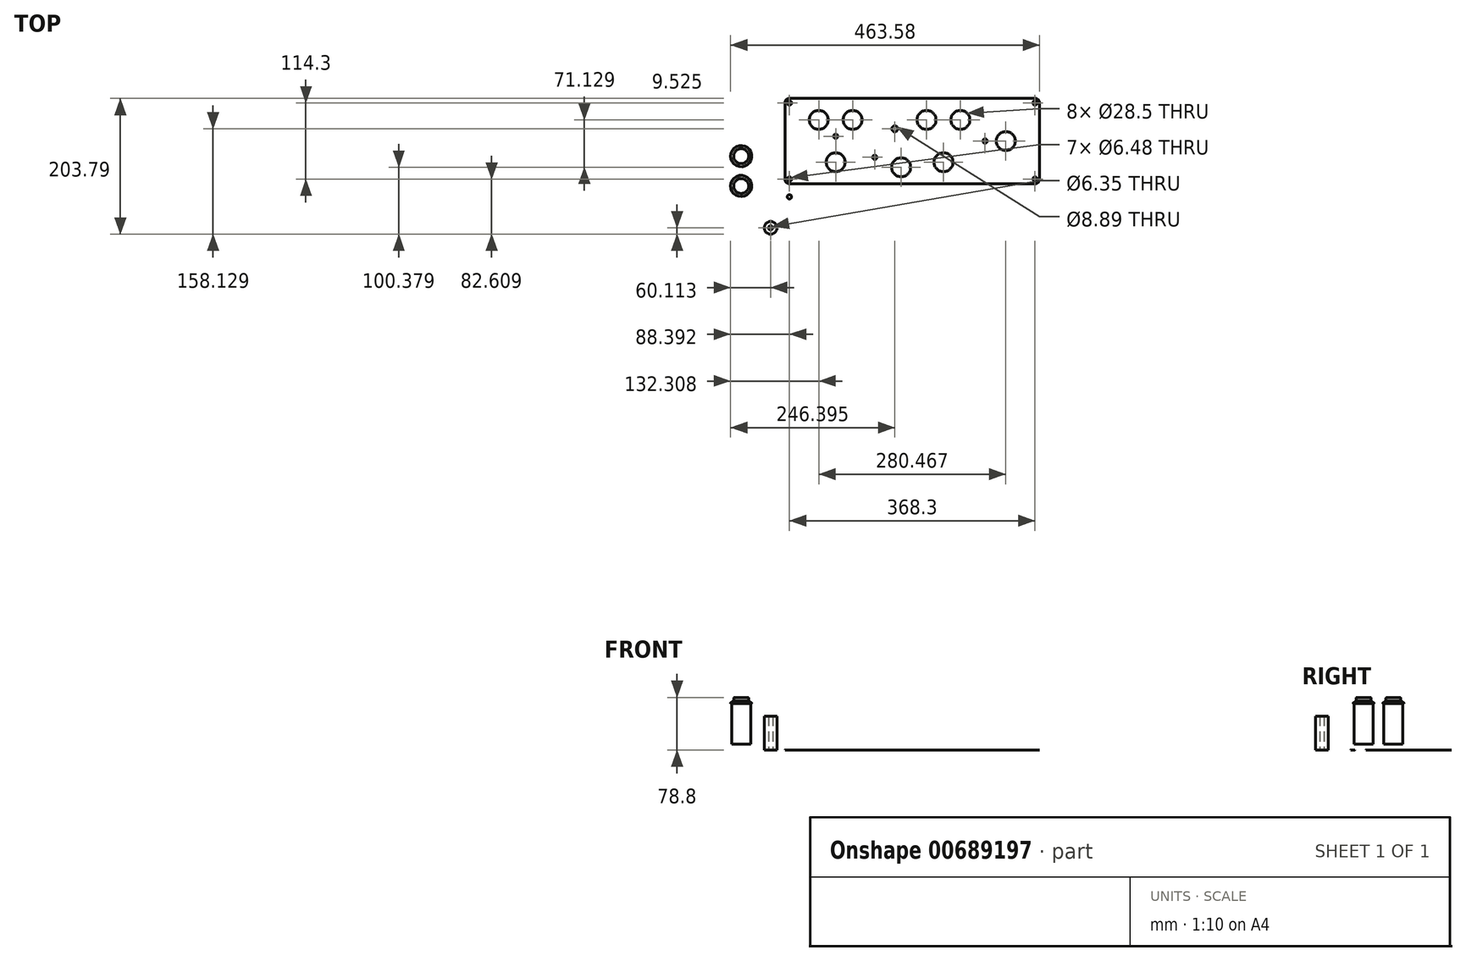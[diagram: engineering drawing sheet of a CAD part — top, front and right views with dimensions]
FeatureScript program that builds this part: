
annotation { "Feature Type Name" : "Feature", "Feature Type Description" : "" }
export const myFeature = defineFeature(function(context is Context, id is Id, definition is map)
    precondition{}
    {
        {
            assignVariable(context, id + "F0", {"name" : "standoff_length", "anyValue" : 50.8 * mm});
        }
        {
            var Q0;
            Q0=qCreatedBy(makeId("Top.planeOp"),FACE);
            var sketch = newSketch(context, id + "F1", { "sketchPlane" : qUnion([Q0])});
            skLineSegment(sketch, "E0.bottom", {"start": v(-110.66, 131.44) * mm, "end": v(271.4, 131.44) * mm});
            skLineSegment(sketch, "E0.top", {"start": v(-110.66, 3.38) * mm, "end": v(271.4, 3.38) * mm});
            skLineSegment(sketch, "E0.left", {"start": v(-110.66, 131.44) * mm, "end": v(-110.66, 3.38) * mm});
            skLineSegment(sketch, "E0.right", {"start": v(271.4, 131.44) * mm, "end": v(271.4, 3.38) * mm});
            skPoint(sketch, "E0.middle", {"position": v(80.37, 67.4) * mm});
            skCircle(sketch, "E1", {"center": v(220.6, 67.4) * mm, "radius": 14.25 * mm});
            skPoint(sketch, "E2", {"position": v(271.4, 67.4) * mm});
            skCircle(sketch, "E3", {"center": v(101.81, 99.16) * mm, "radius": 14.25 * mm});
            skCircle(sketch, "E4", {"center": v(152.61, 99.16) * mm, "radius": 14.25 * mm});
            skCircle(sketch, "E5", {"center": v(127.21, 35.66) * mm, "radius": 14.25 * mm});
            skLineSegment(sketch, "E6", {"start": v(101.81, 99.16) * mm, "end": v(127.21, 35.66) * mm, "construction": true});
            skLineSegment(sketch, "E7", {"start": v(152.61, 99.16) * mm, "end": v(127.21, 35.66) * mm, "construction": true});
            skLineSegment(sketch, "E8", {"start": v(101.81, 99.16) * mm, "end": v(152.61, 99.16) * mm, "construction": true});
            skPoint(sketch, "E9", {"position": v(127.21, 99.16) * mm});
            skCircle(sketch, "E10", {"center": v(63.71, 28.03) * mm, "radius": 14.25 * mm});
            skLineSegment(sketch, "E11", {"start": v(127.21, 99.16) * mm, "end": v(127.21, 35.66) * mm, "construction": true});
            skPoint(sketch, "E12", {"position": v(127.21, 67.4) * mm});
            skLineSegment(sketch, "E13.bottom", {"start": v(-110.66, -137.4) * mm, "end": v(271.4, -137.4) * mm});
            skLineSegment(sketch, "E13.top", {"start": v(-110.66, -9.32) * mm, "end": v(271.4, -9.32) * mm});
            skLineSegment(sketch, "E13.left", {"start": v(-110.66, -137.4) * mm, "end": v(-110.66, -9.32) * mm});
            skLineSegment(sketch, "E13.right", {"start": v(271.4, -137.4) * mm, "end": v(271.4, -9.32) * mm});
            skPoint(sketch, "E13.middle", {"position": v(80.37, -73.36) * mm});
            skLineSegment(sketch, "E14.bottom", {"start": v(-103.78, 124.56) * mm, "end": v(264.52, 124.56) * mm, "construction": true});
            skLineSegment(sketch, "E14.top", {"start": v(-103.78, 10.26) * mm, "end": v(264.52, 10.26) * mm, "construction": true});
            skLineSegment(sketch, "E14.left", {"start": v(-103.78, 124.56) * mm, "end": v(-103.78, 10.26) * mm, "construction": true});
            skLineSegment(sketch, "E14.right", {"start": v(264.52, 124.56) * mm, "end": v(264.52, 10.26) * mm, "construction": true});
            skCircle(sketch, "E15", {"center": v(-103.78, 124.56) * mm, "radius": 3.24 * mm});
            skCircle(sketch, "E16", {"center": v(-103.78, 10.26) * mm, "radius": 3.24 * mm});
            skCircle(sketch, "E17", {"center": v(264.52, 10.26) * mm, "radius": 3.24 * mm});
            skCircle(sketch, "E18", {"center": v(264.52, 124.56) * mm, "radius": 3.24 * mm});
            skLineSegment(sketch, "E19.bottom", {"start": v(-110.66, 3.38) * mm, "end": v(271.4, 3.38) * mm, "construction": true});
            skLineSegment(sketch, "E19.top", {"start": v(-110.66, -9.32) * mm, "end": v(271.4, -9.32) * mm, "construction": true});
            skLineSegment(sketch, "E19.left", {"start": v(-110.66, 3.38) * mm, "end": v(-110.66, -9.32) * mm, "construction": true});
            skLineSegment(sketch, "E19.right", {"start": v(271.4, 3.38) * mm, "end": v(271.4, -9.32) * mm, "construction": true});
            skLineSegment(sketch, "E20", {"start": v(-110.66, -2.97) * mm, "end": v(271.4, -2.97) * mm, "construction": true});
            skCircle(sketch, "E21.MirrorC", {"center": v(-103.78, -16.2) * mm, "radius": 3.24 * mm});
            skCircle(sketch, "E22.MirrorC", {"center": v(-103.78, -130.5) * mm, "radius": 3.24 * mm});
            skCircle(sketch, "E23.MirrorC", {"center": v(264.52, -130.5) * mm, "radius": 3.24 * mm});
            skCircle(sketch, "E24.MirrorC", {"center": v(264.52, -16.2) * mm, "radius": 3.24 * mm});
            skArc(sketch, "E25", {"start": v(-103.78, 131.44) * mm, "mid": v(-108.65, 129.43) * mm, "end": v(-110.66, 124.56) * mm});
            skArc(sketch, "E26", {"start": v(-110.66, 10.26) * mm, "mid": v(-108.65, 5.4) * mm, "end": v(-103.78, 3.38) * mm});
            skArc(sketch, "E27", {"start": v(264.52, 3.38) * mm, "mid": v(269.39, 5.4) * mm, "end": v(271.4, 10.26) * mm});
            skArc(sketch, "E28", {"start": v(271.4, 124.56) * mm, "mid": v(269.39, 129.43) * mm, "end": v(264.52, 131.44) * mm});
            skArc(sketch, "E29.MirrorCS", {"start": v(-110.66, -16.2) * mm, "mid": v(-108.65, -11.34) * mm, "end": v(-103.78, -9.32) * mm});
            skArc(sketch, "E30.MirrorCS", {"start": v(264.52, -9.32) * mm, "mid": v(269.39, -11.34) * mm, "end": v(271.4, -16.2) * mm});
            skArc(sketch, "E31.MirrorCS", {"start": v(271.4, -130.5) * mm, "mid": v(269.39, -135.38) * mm, "end": v(264.52, -137.4) * mm});
            skArc(sketch, "E32.MirrorCS", {"start": v(-103.78, -137.4) * mm, "mid": v(-108.65, -135.38) * mm, "end": v(-110.66, -130.5) * mm});
            skCircle(sketch, "E33", {"center": v(54.23, 85.78) * mm, "radius": 4.45 * mm});
            skCircle(sketch, "E34", {"center": v(189.59, 67.4) * mm, "radius": 3.24 * mm});
            skPoint(sketch, "E34.centerSnap0", {"position": v(264.52, 67.4) * mm});
            skLineSegment(sketch, "E35", {"start": v(-43.99, -40.26) * mm, "end": v(-43.99, -106.45) * mm});
            skPoint(sketch, "E36", {"position": v(-110.66, -73.36) * mm});
            skPoint(sketch, "E37", {"position": v(-43.99, -73.36) * mm});
            skArc(sketch, "E38.0.startCap", {"start": v(-47.16, -40.26) * mm, "mid": v(-43.99, -37.09) * mm, "end": v(-40.81, -40.26) * mm});
            skArc(sketch, "E38.0.endCap", {"start": v(-40.81, -106.45) * mm, "mid": v(-43.99, -109.63) * mm, "end": v(-47.16, -106.45) * mm});
            skLineSegment(sketch, "E38.0.left", {"start": v(-40.81, -40.26) * mm, "end": v(-40.81, -106.45) * mm});
            skLineSegment(sketch, "E38.0.right", {"start": v(-47.16, -40.26) * mm, "end": v(-47.16, -106.45) * mm});
            skLineSegment(sketch, "E39.1.0.0", {"start": v(8.93, -40.26) * mm, "end": v(8.93, -106.45) * mm});
            skArc(sketch, "E39.1.0.1", {"start": v(2.58, -40.26) * mm, "mid": v(5.76, -37.09) * mm, "end": v(8.93, -40.26) * mm});
            skLineSegment(sketch, "E39.1.0.2", {"start": v(2.58, -40.26) * mm, "end": v(2.58, -106.45) * mm});
            skArc(sketch, "E39.1.0.3", {"start": v(8.93, -106.45) * mm, "mid": v(5.76, -109.63) * mm, "end": v(2.58, -106.45) * mm});
            skLineSegment(sketch, "E39.2.0.0", {"start": v(58.68, -40.26) * mm, "end": v(58.68, -106.45) * mm});
            skArc(sketch, "E39.2.0.1", {"start": v(52.33, -40.26) * mm, "mid": v(55.5, -37.09) * mm, "end": v(58.68, -40.26) * mm});
            skLineSegment(sketch, "E39.2.0.2", {"start": v(52.33, -40.26) * mm, "end": v(52.33, -106.45) * mm});
            skArc(sketch, "E39.2.0.3", {"start": v(58.68, -106.45) * mm, "mid": v(55.5, -109.63) * mm, "end": v(52.33, -106.45) * mm});
            skLineSegment(sketch, "E39.3.0.0", {"start": v(108.42, -40.26) * mm, "end": v(108.42, -106.45) * mm});
            skArc(sketch, "E39.3.0.1", {"start": v(102.07, -40.26) * mm, "mid": v(105.24, -37.09) * mm, "end": v(108.42, -40.26) * mm});
            skLineSegment(sketch, "E39.3.0.2", {"start": v(102.07, -40.26) * mm, "end": v(102.07, -106.45) * mm});
            skArc(sketch, "E39.3.0.3", {"start": v(108.42, -106.45) * mm, "mid": v(105.24, -109.63) * mm, "end": v(102.07, -106.45) * mm});
            skLineSegment(sketch, "E39.4.0.0", {"start": v(158.16, -40.26) * mm, "end": v(158.16, -106.45) * mm});
            skArc(sketch, "E39.4.0.1", {"start": v(151.81, -40.26) * mm, "mid": v(154.99, -37.09) * mm, "end": v(158.16, -40.26) * mm});
            skLineSegment(sketch, "E39.4.0.2", {"start": v(151.81, -40.26) * mm, "end": v(151.81, -106.45) * mm});
            skArc(sketch, "E39.4.0.3", {"start": v(158.16, -106.45) * mm, "mid": v(154.99, -109.63) * mm, "end": v(151.81, -106.45) * mm});
            skLineSegment(sketch, "E39.5.0.0", {"start": v(207.9, -40.26) * mm, "end": v(207.9, -106.45) * mm});
            skArc(sketch, "E39.5.0.1", {"start": v(201.56, -40.26) * mm, "mid": v(204.73, -37.09) * mm, "end": v(207.9, -40.26) * mm});
            skLineSegment(sketch, "E39.5.0.2", {"start": v(201.56, -40.26) * mm, "end": v(201.56, -106.45) * mm});
            skArc(sketch, "E39.5.0.3", {"start": v(207.9, -106.45) * mm, "mid": v(204.73, -109.63) * mm, "end": v(201.56, -106.45) * mm});
            skLineSegment(sketch, "E39.direction1", {"start": v(-47.16, -106.45) * mm, "end": v(2.58, -106.45) * mm, "construction": true});
            skLineSegment(sketch, "E40", {"start": v(207.9, -73.36) * mm, "end": v(271.4, -73.36) * mm, "construction": true});
            skLineSegment(sketch, "E41", {"start": v(-110.66, -73.36) * mm, "end": v(-47.16, -73.36) * mm, "construction": true});
            skCircle(sketch, "E42", {"center": v(-59.86, 99.16) * mm, "radius": 14.25 * mm});
            skCircle(sketch, "E43", {"center": v(-9.06, 99.16) * mm, "radius": 14.25 * mm});
            skCircle(sketch, "E44", {"center": v(-34.46, 35.66) * mm, "radius": 14.25 * mm});
            skLineSegment(sketch, "E45", {"start": v(-59.86, 99.16) * mm, "end": v(-34.46, 35.66) * mm, "construction": true});
            skLineSegment(sketch, "E46", {"start": v(-9.06, 99.16) * mm, "end": v(-34.46, 35.66) * mm, "construction": true});
            skLineSegment(sketch, "E47", {"start": v(-59.86, 99.16) * mm, "end": v(-9.06, 99.16) * mm, "construction": true});
            skPoint(sketch, "E48", {"position": v(-34.46, 99.16) * mm});
            skLineSegment(sketch, "E49", {"start": v(-34.46, 99.16) * mm, "end": v(-34.46, 35.66) * mm, "construction": true});
            skPoint(sketch, "E50", {"position": v(-34.46, 67.4) * mm});
            skCircle(sketch, "E51", {"center": v(-34.46, 74.6) * mm, "radius": 3.24 * mm});
            skCircle(sketch, "E52", {"center": v(24.13, 43) * mm, "radius": 3.24 * mm});
            skCircle(sketch, "E53.MirrorC", {"center": v(24.13, -48.96) * mm, "radius": 3.24 * mm});
            skCircle(sketch, "E54.MirrorC", {"center": v(-34.46, -80.55) * mm, "radius": 3.24 * mm});
            skCircle(sketch, "E55.MirrorC", {"center": v(189.59, -73.36) * mm, "radius": 3.24 * mm});
            skSolve(sketch);
        }
        {
            var Q0;
            Q0=makeQuery(id+"F1.imprint","IMPRINT",FACE,{"disambiguationData":[TD([[makeQuery(id+"F1.imprint","IMPRINT",EDGE,{"derivedFrom":sQuery(id+"F1.wireOp",EDGE,"E1")}),-1.0]])]});
            var Q1;
            Q1=makeQuery(id+"F1.imprint","IMPRINT",FACE,{"disambiguationData":[TD([[makeQuery(id+"F1.imprint","IMPRINT",EDGE,{"derivedFrom":sQuery(id+"F1.wireOp",EDGE,"E21.MirrorC")}),1.0]])]});
            extrude(context, id + "F2", {"entities" : qUnion([Q0, Q1]), "oppositeDirection" : true, "depth" : 1 / 203.2 * mm, "offsetDistance" : 25.4 * mm});
        }
        {
            var Q0;
            Q0=qCreatedBy(makeId("Top.planeOp"),FACE);
            var sketch = newSketch(context, id + "F3", { "sketchPlane" : qUnion([Q0])});
            skCircle(sketch, "E56", {"center": v(-132.06, -62.82) * mm, "radius": 3.18 * mm});
            skCircle(sketch, "E57", {"center": v(-132.06, -62.82) * mm, "radius": 9.53 * mm});
            skSolve(sketch);
        }
        {
            var Q0;
            Q0=makeQuery(id+"F3.imprint","IMPRINT",FACE,{"disambiguationData":[TD([[makeQuery(id+"F3.imprint","IMPRINT",EDGE,{"derivedFrom":sQuery(id+"F3.wireOp",EDGE,"E56")}),-1.0]])]});
            extrude(context, id + "F4", {"entities" : qUnion([Q0]), "depth" : getVariable(context, 'standoff_length'), "offsetDistance" : 25.4 * mm});
        }
        {
            var Q0;
            Q0=qCreatedBy(makeId("Front.planeOp"),FACE);
            var sketch = newSketch(context, id + "F5", { "sketchPlane" : qUnion([Q0])});
            skLineSegment(sketch, "E58", {"start": v(-176.24, 73.72) * mm, "end": v(-176.24, 8.72) * mm});
            skLineSegment(sketch, "E59", {"start": v(-176.24, 73.72) * mm, "end": v(-165.06, 73.72) * mm});
            skLineSegment(sketch, "E60", {"start": v(-164.26, 73.44) * mm, "end": v(-159.84, 69.9) * mm});
            skLineSegment(sketch, "E61", {"start": v(-159.84, 69.9) * mm, "end": v(-176.24, 69.9) * mm});
            skPoint(sketch, "E62.visualSharp", {"position": v(-164.61, 73.72) * mm});
            skArc(sketch, "E62.filletArc", {"start": v(-164.26, 73.44) * mm, "mid": v(-164.64, 73.64) * mm, "end": v(-165.06, 73.72) * mm});
            skLineSegment(sketch, "E63", {"start": v(-161.99, 69.9) * mm, "end": v(-161.99, 8.72) * mm});
            skLineSegment(sketch, "E64", {"start": v(-161.99, 8.72) * mm, "end": v(-176.24, 8.72) * mm});
            skLineSegment(sketch, "E65", {"start": v(-176.24, 73.72) * mm, "end": v(-176.24, 78.8) * mm});
            skLineSegment(sketch, "E66", {"start": v(-176.24, 78.8) * mm, "end": v(-165.06, 78.8) * mm});
            skLineSegment(sketch, "E67", {"start": v(-165.06, 78.8) * mm, "end": v(-165.06, 73.72) * mm});
            skSolve(sketch);
        }
        {
            var Q0;
            {var subQ3=sQuery(id+"F5.wireOp",EDGE,"E59");Q0=makeQuery(id+"F5.imprint","IMPRINT",FACE,{"disambiguationData":[TD([[makeQuery(id+"F5.imprint","IMPRINT",EDGE,{"derivedFrom":subQ3}),-1.0]])]});}
            var Q1;
            {var subQ4=sQuery(id+"F5.wireOp",EDGE,"E63");Q1=makeQuery(id+"F5.imprint","IMPRINT",FACE,{"disambiguationData":[TD([[makeQuery(id+"F5.imprint","IMPRINT",EDGE,{"derivedFrom":subQ4}),-1.0]])]});}
            var Q2;
            Q2=makeQuery(id+"F5.imprint","IMPRINT",FACE,{"disambiguationData":[TD([[makeQuery(id+"F5.imprint","IMPRINT",EDGE,{"derivedFrom":sQuery(id+"F5.wireOp",EDGE,"E59")}),1.0]])]});
            var Q3;
            Q3=sQuery(id+"F5.wireOp",EDGE,"E58");
            revolve(context, id + "F6", {"entities" : qUnion([Q0, Q1, Q2]), "axis" : qUnion([Q3]), "revolveType" : RevolveType.FULL});
        }
        {
            var Q0;
            Q0=makeQuery(id+"F6.opRevolve","SWEPT_FACE",FACE,{"disambiguationData":[OSD([sQuery(id+"F5.wireOp",EDGE,"E66")])]});
            fillet(context, id + "F7", {"entities" : qUnion([Q0]), "radius" : 1.27 * mm, "tangentPropagation" : true, "allowEdgeOverflow" : false});
        }
        {
            var Q0;
            Q0=makeQuery(id+"F6.opRevolve","SWEPT_EDGE",EDGE,{"disambiguationData":[OSD([sQuery(id+"F5.wireOp",EDGE,"E60"),sQuery(id+"F5.wireOp",EDGE,"E61")])]});
            fillet(context, id + "F8", {"entities" : qUnion([Q0]), "radius" : 0.25 * mm, "tangentPropagation" : true, "allowEdgeOverflow" : false});
        }
        {
            var Q0;
            Q0=makeQuery(id+"F6.opRevolve","SWEPT_BODY",BODY,{"disambiguationData":[OSD([sQuery(id+"F5.wireOp",EDGE,"E58"),sQuery(id+"F5.wireOp",EDGE,"E60"),sQuery(id+"F5.wireOp",EDGE,"E61"),sQuery(id+"F5.wireOp",EDGE,"E62.filletArc"),sQuery(id+"F5.wireOp",EDGE,"E63"),sQuery(id+"F5.wireOp",EDGE,"E64"),sQuery(id+"F5.wireOp",EDGE,"E65"),sQuery(id+"F5.wireOp",EDGE,"E66"),sQuery(id+"F5.wireOp",EDGE,"E67")])]});
            transform(context, id + "F9", {"entities" : qUnion([Q0]), "transformType" : TransformType.TRANSLATION_3D, "dx" : 0 * mm, "dy" : 44.7 * mm, "dz" : 0 * mm, "makeCopy" : true});
        }
    });
